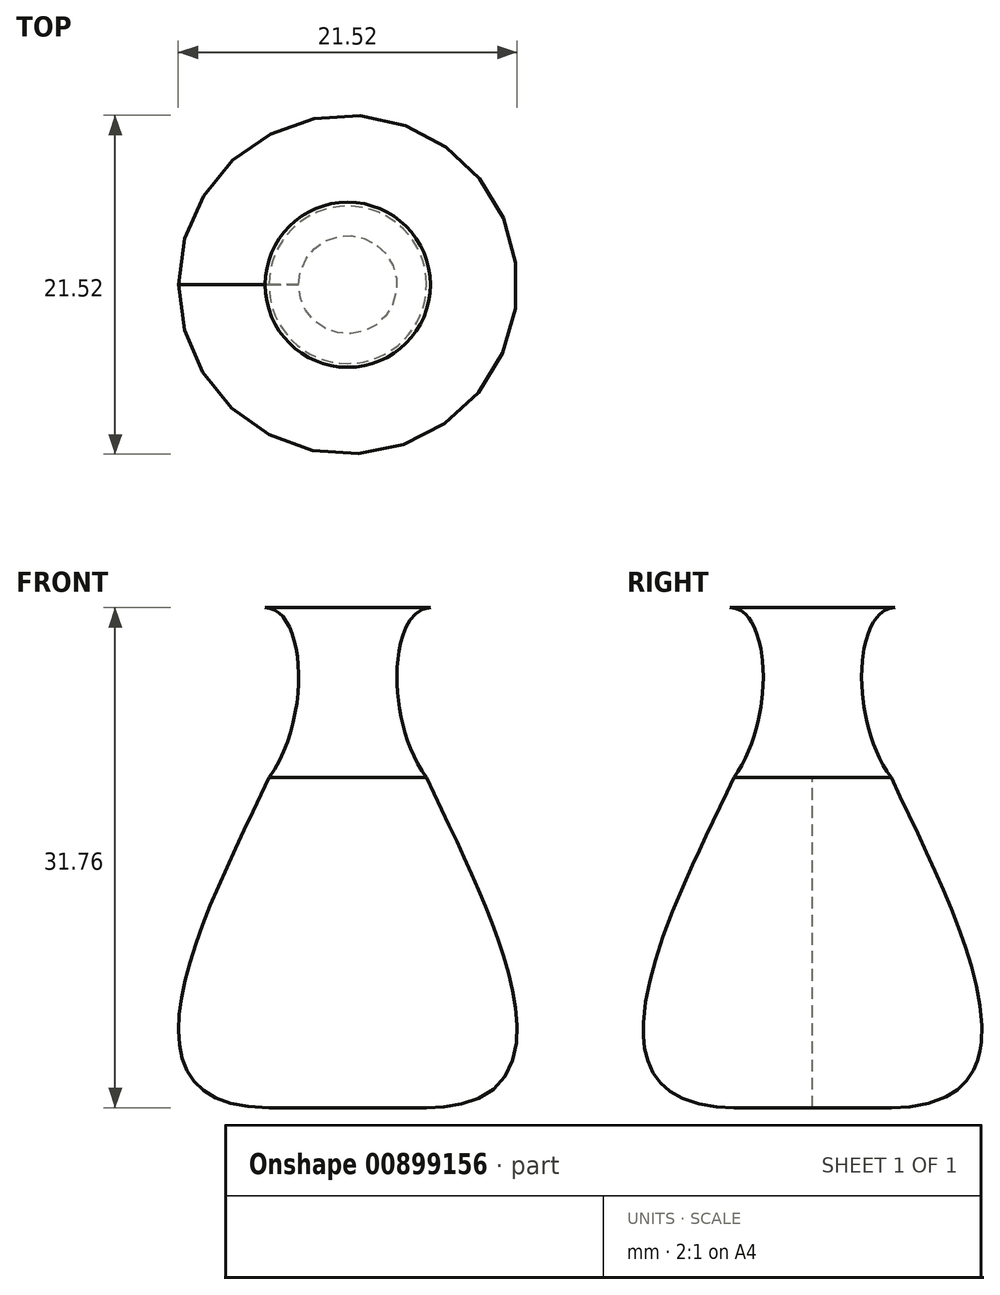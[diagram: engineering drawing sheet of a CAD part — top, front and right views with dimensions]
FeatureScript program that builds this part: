
annotation { "Feature Type Name" : "Feature", "Feature Type Description" : "" }
export const myFeature = defineFeature(function(context is Context, id is Id, definition is map)
    precondition{}
    {
        {
            var Q0;
            Q0=qCreatedBy(makeId("Front.planeOp"),FACE);
            var sketch = newSketch(context, id + "F0", { "sketchPlane" : qUnion([Q0])});
            skLineSegment(sketch, "E0", {"start": v(0, 0) * mm, "end": v(5, 0) * mm});
            skFitSpline(sketch, "E1", {"points": [v(5, 0) * mm, v(5, 20.96) * mm], "startDerivative": vector(32.6, 0) * mm, "endDerivative": vector(-11.06, 23.62) * mm});
            skFitSpline(sketch, "E2", {"points": [v(5, 20.96) * mm, v(5.24, 31.76) * mm], "startDerivative": vector(-8.4, 11.81) * mm, "endDerivative": vector(7.53, 0) * mm});
            skLineSegment(sketch, "E3", {"start": v(5.24, 31.76) * mm, "end": v(0, 31.76) * mm});
            skFitSpline(sketch, "E4.MirrorCS", {"points": [v(-5, 20.96) * mm, v(-5.24, 31.76) * mm], "startDerivative": vector(8.4, 11.81) * mm, "endDerivative": vector(-7.53, 0) * mm});
            skFitSpline(sketch, "E5.MirrorCS", {"points": [v(-5, 0) * mm, v(-5, 20.96) * mm], "startDerivative": vector(-32.6, 0) * mm, "endDerivative": vector(11.06, 23.62) * mm});
            skLineSegment(sketch, "E6.MirrorCS", {"start": v(0, 0) * mm, "end": v(-5, 0) * mm});
            skLineSegment(sketch, "E7.MirrorCS", {"start": v(-5.24, 31.76) * mm, "end": v(0, 31.76) * mm});
            skLineSegment(sketch, "E8", {"start": v(0, 31.76) * mm, "end": v(0, 0) * mm, "construction": true});
            skSolve(sketch);
        }
        {
            var Q0;
            Q0=makeQuery(id+"F0.imprint","IMPRINT",FACE,{"disambiguationData":[TD([[makeQuery(id+"F0.imprint","IMPRINT",EDGE,{"derivedFrom":sQuery(id+"F0.wireOp",EDGE,"E0")}),1.0]])]});
            var Q1;
            Q1=sQuery(id+"F0.wireOp",EDGE,"E3");
            var Q2;
            Q2=sQuery(id+"F0.wireOp",EDGE,"E2");
            var Q3;
            Q3=sQuery(id+"F0.wireOp",EDGE,"E1");
            var Q4;
            Q4=sQuery(id+"F0.wireOp",EDGE,"E0");
            var Q5;
            Q5=sQuery(id+"F0.wireOp",EDGE,"E8");
            revolve(context, id + "F1", {"bodyType" : ToolBodyType.SURFACE, "surfaceOperationType" : NewSurfaceOperationType.NEW, "entities" : qUnion([Q0]), "surfaceEntities" : qUnion([Q1, Q2, Q3, Q4]), "axis" : qUnion([Q5]), "revolveType" : RevolveType.FULL});
        }
    });
